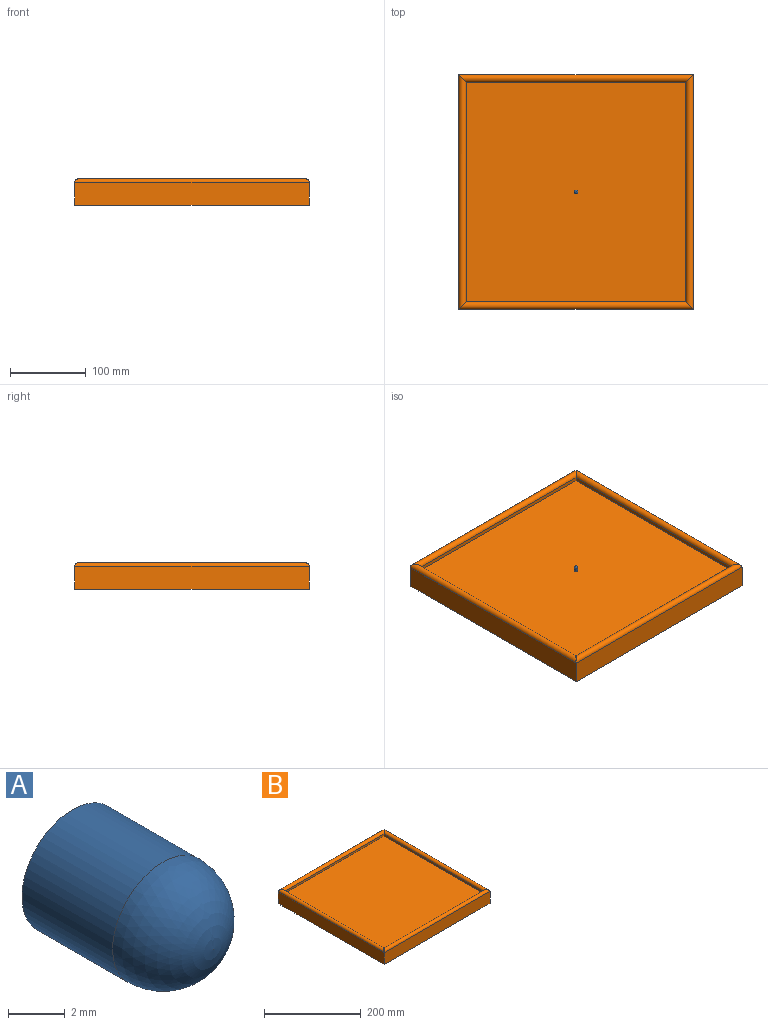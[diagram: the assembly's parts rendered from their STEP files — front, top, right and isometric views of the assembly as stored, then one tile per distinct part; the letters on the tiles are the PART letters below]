
ASSEMBLY  parts=2 mates=1
PART A: 3 faces, bbox 5x7x5 mm
  f0: cylinder r=2.5mm len=5mm, axis (0,1,0), area 70.7mm2, adj f1,f2
  f1: plane 5x5mm, normal (0,1,0), area 19.6mm2, adj f0
  f2: sphere r=2.5mm, area 39.3mm2, adj f0
PART B: 14 faces, bbox 310x310x35 mm
  f0: plane 290x5mm, normal (1,0,0), area 1450mm2, adj f1,f7,f9,f10
  f1: plane 290x290mm, normal (0,0,1), area 84100mm2, adj f0,f7,f8,f9
  f2: plane 310x30mm, normal (0,1,0), area 9300mm2, adj f3,f5,f6,f12
  f3: plane 310x30mm, normal (-1,0,0), area 9300mm2, adj f2,f4,f6,f10
  f4: plane 310x30mm, normal (0,-1,0), area 9300mm2, adj f3,f5,f6,f11
  f5: plane 310x30mm, normal (1,0,0), area 9300mm2, adj f2,f4,f6,f13
  f6: plane 310x310mm, normal (0,0,-1), area 96100mm2, adj f2,f3,f4,f5
  f7: plane 290x5mm, normal (0,1,0), area 1450mm2, adj f0,f1,f8,f11
  f8: plane 290x5mm, normal (-1,0,0), area 1450mm2, adj f1,f7,f9,f13
  f9: plane 290x5mm, normal (0,-1,0), area 1450mm2, adj f0,f1,f8,f12
  f10: cylinder r=5mm len=310mm, axis (0,1,0), area 4712.4mm2, adj f0,f3,f11,f12
  f11: cylinder r=5mm len=310mm, axis (-1,0,0), area 4712.4mm2, adj f4,f7,f10,f13
  f12: cylinder r=5mm len=310mm, axis (1,0,0), area 4712.4mm2, adj f2,f9,f10,f13
  f13: cylinder r=5mm len=310mm, axis (0,-1,0), area 4712.4mm2, adj f5,f8,f11,f12
PLACE A rot(axis=(-1,0,0),90deg) t=(-54.39,90.74,-1.32)mm
PLACE B t=(-209.39,-64.26,-26.32)mm
MATE planar A.f0 <-> B.f1  axis (0,0,-1) through (-54.39,90.74,-1.32)mm
